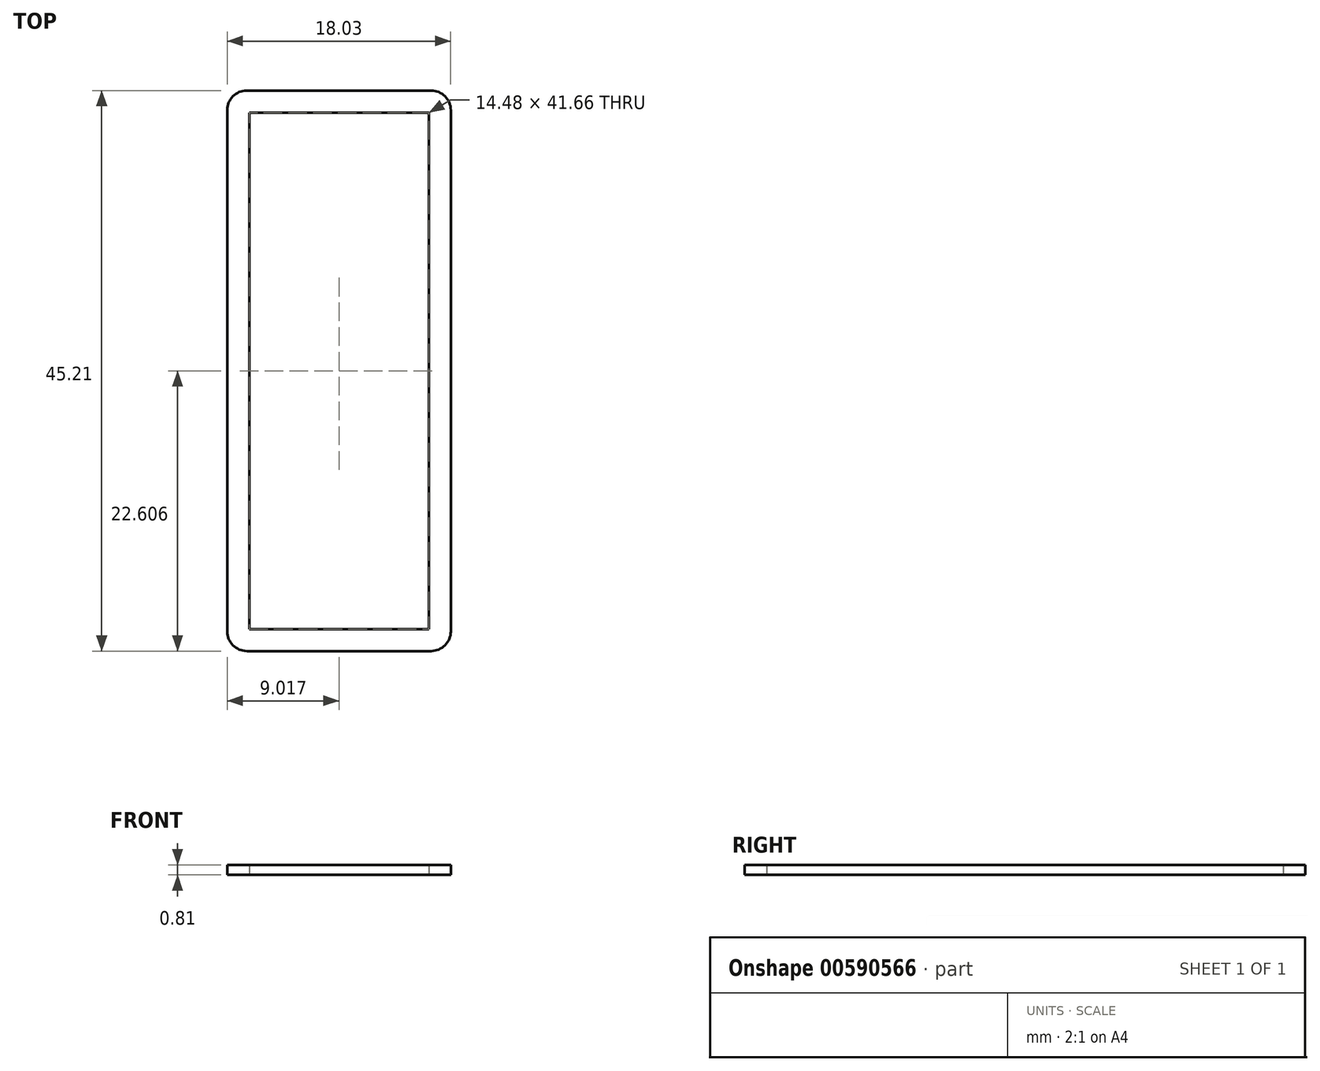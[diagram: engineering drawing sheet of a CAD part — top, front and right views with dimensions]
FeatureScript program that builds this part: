
annotation { "Feature Type Name" : "Feature", "Feature Type Description" : "" }
export const myFeature = defineFeature(function(context is Context, id is Id, definition is map)
    precondition{}
    {
        {
            var Q0;
            Q0=qCreatedBy(makeId("Top.planeOp"),FACE);
            var sketch = newSketch(context, id + "F0", { "sketchPlane" : qUnion([Q0])});
            skLineSegment(sketch, "E0.bottom", {"start": v(1.59, 0) * mm, "end": v(16.45, 0) * mm});
            skLineSegment(sketch, "E0.top", {"start": v(1.59, 45.21) * mm, "end": v(16.45, 45.21) * mm});
            skLineSegment(sketch, "E0.left", {"start": v(0, 1.59) * mm, "end": v(0, 43.62) * mm});
            skLineSegment(sketch, "E0.right", {"start": v(18.03, 1.59) * mm, "end": v(18.03, 43.62) * mm});
            skLineSegment(sketch, "E1.0", {"start": v(1.78, 43.43) * mm, "end": v(16.26, 43.43) * mm});
            skLineSegment(sketch, "E1.1", {"start": v(1.78, 1.78) * mm, "end": v(1.78, 43.43) * mm});
            skLineSegment(sketch, "E1.2", {"start": v(1.78, 1.78) * mm, "end": v(16.26, 1.78) * mm});
            skLineSegment(sketch, "E1.3", {"start": v(16.26, 1.78) * mm, "end": v(16.26, 43.43) * mm});
            skPoint(sketch, "E2.visualSharp", {"position": v(18.03, 0) * mm});
            skArc(sketch, "E2.filletArc", {"start": v(16.45, 0) * mm, "mid": v(17.57, 0.46) * mm, "end": v(18.03, 1.59) * mm});
            skPoint(sketch, "E3.visualSharp", {"position": v(0, 0) * mm});
            skArc(sketch, "E3.filletArc", {"start": v(0, 1.59) * mm, "mid": v(0.46, 0.46) * mm, "end": v(1.59, 0) * mm});
            skPoint(sketch, "E4.visualSharp", {"position": v(18.03, 45.21) * mm});
            skArc(sketch, "E4.filletArc", {"start": v(18.03, 43.62) * mm, "mid": v(17.57, 44.75) * mm, "end": v(16.45, 45.21) * mm});
            skPoint(sketch, "E5.visualSharp", {"position": v(0, 45.21) * mm});
            skArc(sketch, "E5.filletArc", {"start": v(1.59, 45.21) * mm, "mid": v(0.46, 44.75) * mm, "end": v(0, 43.62) * mm});
            skSolve(sketch);
        }
        {
            var Q0;
            Q0=qSketchRegion(id+"F0",true);
            extrude(context, id + "F1", {"entities" : qUnion([Q0]), "depth" : 0.81 * mm, "offsetDistance" : 25 * mm});
        }
    });
